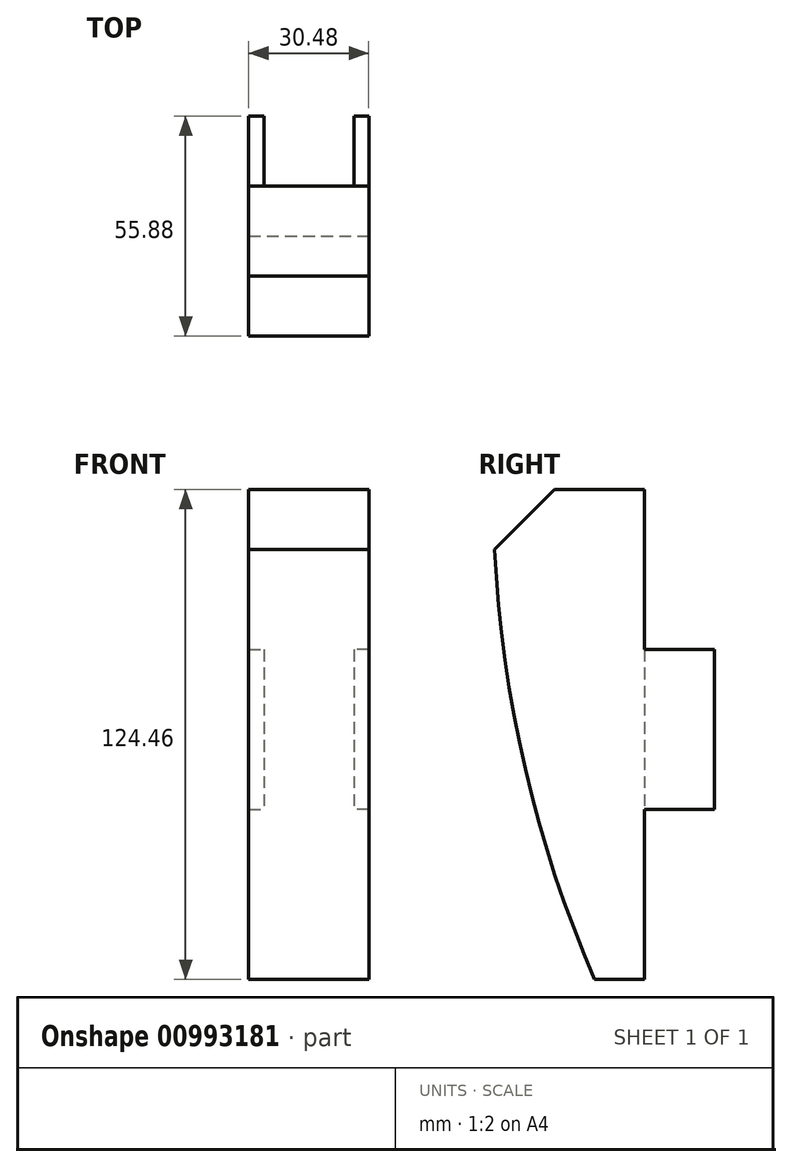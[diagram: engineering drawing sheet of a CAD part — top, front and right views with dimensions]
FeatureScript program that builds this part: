
annotation { "Feature Type Name" : "Feature", "Feature Type Description" : "" }
export const myFeature = defineFeature(function(context is Context, id is Id, definition is map)
    precondition{}
    {
        {
            var Q0;
            Q0=qCreatedBy(makeId("Front.planeOp"),FACE);
            var sketch = newSketch(context, id + "F0", { "sketchPlane" : qUnion([Q0])});
            skLineSegment(sketch, "E0.bottom", {"start": v(-55.75, 42.35) * mm, "end": v(-25.27, 42.35) * mm});
            skLineSegment(sketch, "E0.top", {"start": v(-55.75, -33.85) * mm, "end": v(-25.27, -33.85) * mm});
            skLineSegment(sketch, "E0.left", {"start": v(-55.75, 42.35) * mm, "end": v(-55.75, -33.85) * mm});
            skLineSegment(sketch, "E0.right", {"start": v(-25.27, 42.35) * mm, "end": v(-25.27, -33.85) * mm});
            skPoint(sketch, "E1.startSnap0", {"position": v(-55.75, 4.25) * mm});
            skPoint(sketch, "E2.startSnap0", {"position": v(-25.27, 4.25) * mm});
            skLineSegment(sketch, "E3.bottom", {"start": v(-25.27, 24.57) * mm, "end": v(-29.08, 24.57) * mm});
            skLineSegment(sketch, "E3.top", {"start": v(-25.27, -16.07) * mm, "end": v(-29.08, -16.07) * mm});
            skLineSegment(sketch, "E3.left", {"start": v(-25.27, 24.57) * mm, "end": v(-25.27, -16.07) * mm});
            skLineSegment(sketch, "E3.right", {"start": v(-29.08, 24.57) * mm, "end": v(-29.08, -16.07) * mm});
            skPoint(sketch, "E3.middle", {"position": v(-27.17, 4.25) * mm});
            skLineSegment(sketch, "E4.bottom", {"start": v(-55.75, 24.57) * mm, "end": v(-51.94, 24.57) * mm});
            skLineSegment(sketch, "E4.top", {"start": v(-55.75, -16.07) * mm, "end": v(-51.94, -16.07) * mm});
            skLineSegment(sketch, "E4.left", {"start": v(-55.75, 24.57) * mm, "end": v(-55.75, -16.07) * mm});
            skLineSegment(sketch, "E4.right", {"start": v(-51.94, 24.57) * mm, "end": v(-51.94, -16.07) * mm});
            skPoint(sketch, "E4.middle", {"position": v(-53.84, 4.25) * mm});
            skSolve(sketch);
        }
        {
            var Q0;
            Q0=makeQuery(id+"F0.imprint","IMPRINT",FACE,{"disambiguationData":[TD([[makeQuery(id+"F0.imprint","IMPRINT",EDGE,{"derivedFrom":sQuery(id+"F0.wireOp",EDGE,"E0.bottom")}),-1.0]])]});
            var Q1;
            Q1=makeQuery(id+"F0.imprint","IMPRINT",FACE,{"disambiguationData":[TD([[makeQuery(id+"F0.imprint","IMPRINT",EDGE,{"derivedFrom":sQuery(id+"F0.wireOp",EDGE,"E0.left")}),-1.0]])]});
            var Q2;
            Q2=makeQuery(id+"F0.imprint","IMPRINT",FACE,{"disambiguationData":[TD([[makeQuery(id+"F0.imprint","IMPRINT",EDGE,{"derivedFrom":sQuery(id+"F0.wireOp",EDGE,"E0.right")}),1.0]])]});
            extrude(context, id + "F1", {"entities" : qUnion([Q0, Q1, Q2]), "depth" : 7.62 * mm, "offsetDistance" : 25.4 * mm});
        }
        {
            var Q0;
            Q0=makeQuery(id+"F0.imprint","IMPRINT",FACE,{"disambiguationData":[TD([[makeQuery(id+"F0.imprint","IMPRINT",EDGE,{"derivedFrom":sQuery(id+"F0.wireOp",EDGE,"E4.bottom")}),-1.0]])]});
            var Q1;
            Q1=makeQuery(id+"F0.imprint","IMPRINT",FACE,{"disambiguationData":[TD([[makeQuery(id+"F0.imprint","IMPRINT",EDGE,{"derivedFrom":sQuery(id+"F0.wireOp",EDGE,"E3.bottom")}),1.0]])]});
            extrude(context, id + "F2", {"entities" : qUnion([Q0, Q1]), "operationType" : NewBodyOperationType.ADD, "oppositeDirection" : true, "depth" : 17.78 * mm, "offsetDistance" : 25.4 * mm, "hasSecondDirection" : true, "secondDirectionOppositeDirection" : false, "secondDirectionDepth" : 7.62 * mm});
        }
        {
            var Q0;
            {var subQ0=sQuery(id+"F0.wireOp",EDGE,"E3.left");var subQ1=sQuery(id+"F0.wireOp",EDGE,"E0.right");Q0=makeQuery(id+"F2.boolean.opBoolean","MERGE",FACE,{"derivedFrom":[makeQuery(id+"F1.opExtrude","SWEPT_FACE",FACE,{"disambiguationData":[OSD([subQ1]),TDD([makeQuery(id+"F0.imprint","IMPRINT",EDGE,{"disambiguationData":[TD([[makeQuery(id+"F0.imprint","INTERSECT",VERTEX,{"derivedFrom":[sQuery(id+"F0.wireOp",EDGE,"E0.bottom"),subQ1]}),-1.0]])],"derivedFrom":subQ1})])]}),makeQuery(id+"F1.opExtrude","SWEPT_FACE",FACE,{"disambiguationData":[OSD([subQ1]),TDD([makeQuery(id+"F0.imprint","IMPRINT",EDGE,{"disambiguationData":[TD([[makeQuery(id+"F0.imprint","INTERSECT",VERTEX,{"derivedFrom":[sQuery(id+"F0.wireOp",EDGE,"E0.top"),subQ1]}),1.0]])],"derivedFrom":subQ1})])]}),makeQuery(id+"F2.opExtrude","SWEPT_FACE",FACE,{"disambiguationData":[OSD([subQ0])]})]});}
            var sketch = newSketch(context, id + "F3", { "sketchPlane" : qUnion([Q0])});
            skLineSegment(sketch, "E5", {"start": v(0, 42.35) * mm, "end": v(0, 67.75) * mm});
            skLineSegment(sketch, "E6", {"start": v(0, 67.75) * mm, "end": v(-20.32, 67.75) * mm});
            skLineSegment(sketch, "E7", {"start": v(0, -33.85) * mm, "end": v(0, -59.25) * mm});
            skLineSegment(sketch, "E8", {"start": v(-20.32, 67.75) * mm, "end": v(-38.1, 49.97) * mm});
            skLineSegment(sketch, "E9", {"start": v(0, -59.25) * mm, "end": v(-12.7, -59.25) * mm});
            skArc(sketch, "E10", {"start": v(-38.1, 49.97) * mm, "mid": v(-30.34, -5.8) * mm, "end": v(-12.7, -59.25) * mm});
            skSolve(sketch);
        }
        {
            var Q0;
            Q0=makeQuery(id+"F3.imprint","IMPRINT",FACE,{"disambiguationData":[TD([[makeQuery(id+"F3.imprint","IMPRINT",EDGE,{"derivedFrom":sQuery(id+"F3.wireOp",EDGE,"E5")}),1.0]])]});
            extrude(context, id + "F4", {"entities" : qUnion([Q0]), "operationType" : NewBodyOperationType.ADD, "oppositeDirection" : true, "depth" : 30.48 * mm, "offsetDistance" : 25.4 * mm});
        }
        {
            var Q0;
            {var subQ0=sQuery(id+"F0.wireOp",EDGE,"E3.left");var subQ1=sQuery(id+"F0.wireOp",EDGE,"E0.right");var subQ2=sQuery(id+"F0.wireOp",EDGE,"E0.top");var subQ3=sQuery(id+"F0.wireOp",EDGE,"E0.bottom");Q0=makeQuery(id+"F4.boolean.opBoolean","MERGE",FACE,{"derivedFrom":[makeQuery(id+"F2.boolean.opBoolean","MERGE",FACE,{"derivedFrom":[makeQuery(id+"F1.opExtrude","SWEPT_FACE",FACE,{"disambiguationData":[OSD([subQ1]),TDD([makeQuery(id+"F0.imprint","IMPRINT",EDGE,{"disambiguationData":[TD([[makeQuery(id+"F0.imprint","INTERSECT",VERTEX,{"derivedFrom":[subQ3,subQ1]}),-1.0]])],"derivedFrom":subQ1})])]}),makeQuery(id+"F1.opExtrude","SWEPT_FACE",FACE,{"disambiguationData":[OSD([subQ1]),TDD([makeQuery(id+"F0.imprint","IMPRINT",EDGE,{"disambiguationData":[TD([[makeQuery(id+"F0.imprint","INTERSECT",VERTEX,{"derivedFrom":[subQ2,subQ1]}),1.0]])],"derivedFrom":subQ1})])]}),makeQuery(id+"F2.opExtrude","SWEPT_FACE",FACE,{"disambiguationData":[OSD([subQ0])]})]}),makeQuery(id+"F4.opExtrude","CAP_FACE",FACE,{"disambiguationData":[OSD([subQ3,subQ2,subQ1,subQ0,sQuery(id+"F3.wireOp",EDGE,"E5"),sQuery(id+"F3.wireOp",EDGE,"E6"),sQuery(id+"F3.wireOp",EDGE,"E7"),sQuery(id+"F3.wireOp",EDGE,"txeqDOJH-kMNY-swYj-O1Tx-qxdqHIPKTNKk")])],"isStart":true})]});}
            var sketch = newSketch(context, id + "F5", { "sketchPlane" : qUnion([Q0])});
            skLineSegment(sketch, "E11.bottom", {"start": v(0, 67.75) * mm, "end": v(-20.43, 67.75) * mm});
            skLineSegment(sketch, "E11.left", {"start": v(0, 67.75) * mm, "end": v(0, 65.2) * mm});
            skLineSegment(sketch, "E12", {"start": v(0, 65.2) * mm, "end": v(-22.86, 65.2) * mm});
            skSolve(sketch);
        }
        {
            var Q0;
            {var subQ4=sQuery(id+"F5.wireOp",EDGE,"E11.top");Q0=makeQuery(id+"F5.imprint","IMPRINT",FACE,{"disambiguationData":[TD([[makeQuery(id+"F5.imprint","IMPRINT",EDGE,{"derivedFrom":subQ4}),-1.0]])]});}
            var Q1;
            {var subQ0=sQuery(id+"F5.wireOp",EDGE,"E11.left");Q1=makeQuery(id+"F5.imprint","IMPRINT",FACE,{"disambiguationData":[TD([[makeQuery(id+"F5.imprint","IMPRINT",EDGE,{"derivedFrom":subQ0}),-1.0]])]});}
            extrude(context, id + "F6", {"entities" : qUnion([Q0, Q1]), "operationType" : NewBodyOperationType.REMOVE, "oppositeDirection" : true, "depth" : 50.8 * mm, "offsetDistance" : 25.4 * mm});
        }
    });
